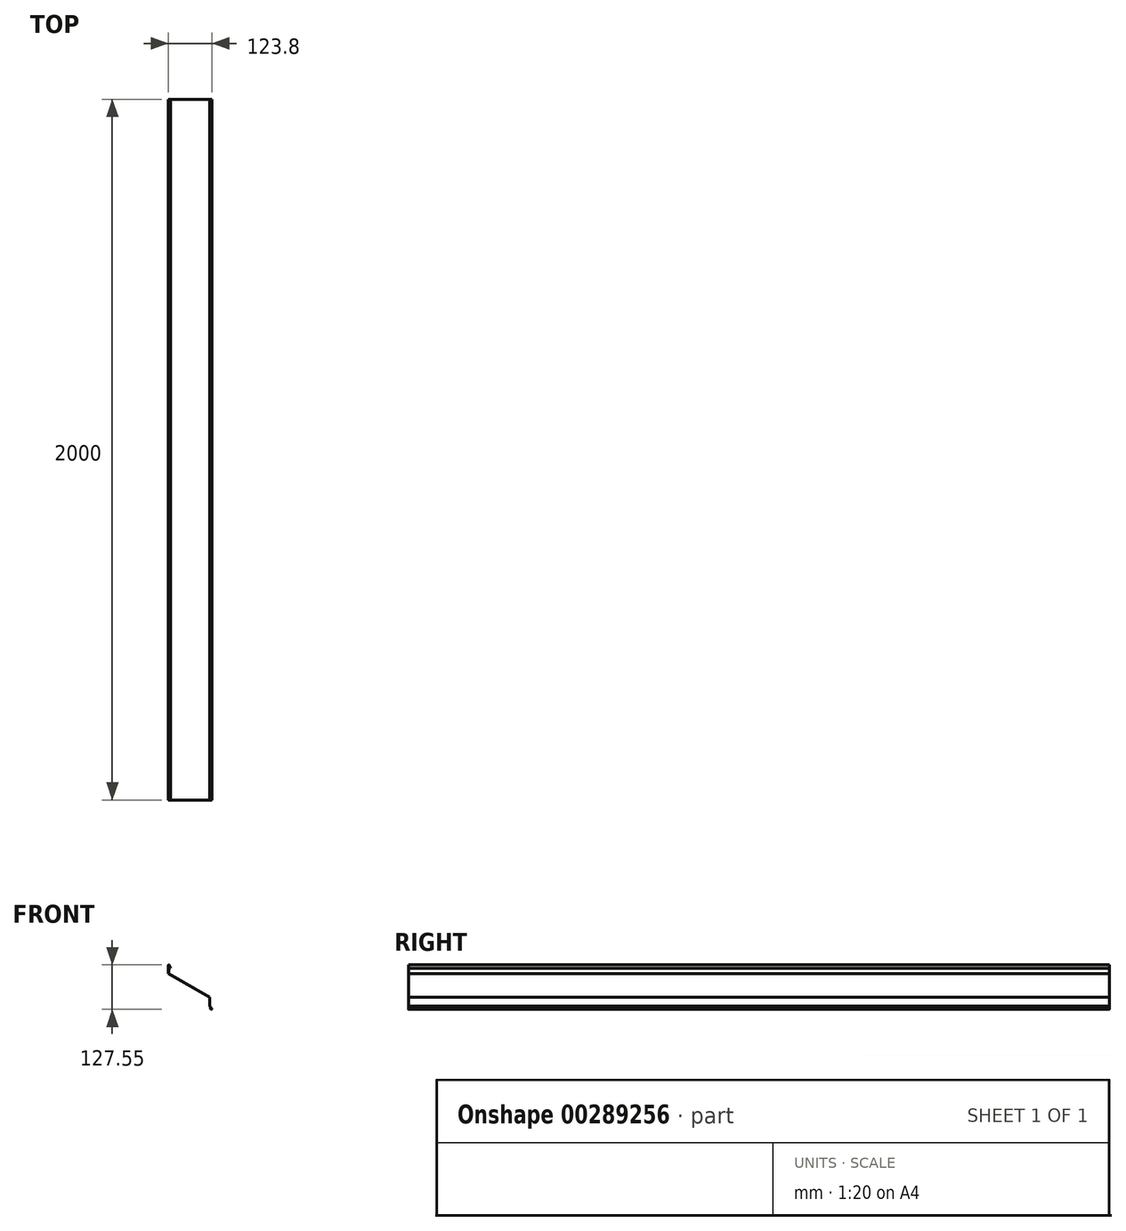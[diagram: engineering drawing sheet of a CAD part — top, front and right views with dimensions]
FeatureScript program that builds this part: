
annotation { "Feature Type Name" : "Feature", "Feature Type Description" : "" }
export const myFeature = defineFeature(function(context is Context, id is Id, definition is map)
    precondition{}
    {
        {
            var Q0;
            Q0=qCreatedBy(makeId("Front.planeOp"),FACE);
            var sketch = newSketch(context, id + "F0", { "sketchPlane" : qUnion([Q0])});
            skLineSegment(sketch, "E0", {"start": v(0, -1.3) * mm, "end": v(0, -25) * mm});
            skLineSegment(sketch, "E1", {"start": v(0, -25) * mm, "end": v(117, -92.55) * mm});
            skLineSegment(sketch, "E2", {"start": v(117, -92.55) * mm, "end": v(117, -117.55) * mm});
            skLineSegment(sketch, "E3", {"start": v(-1, -1.3) * mm, "end": v(-1, -25.58) * mm});
            skLineSegment(sketch, "E4", {"start": v(-1, -25.58) * mm, "end": v(116, -93.13) * mm});
            skLineSegment(sketch, "E5", {"start": v(116, -93.13) * mm, "end": v(116, -117.87) * mm});
            skLineSegment(sketch, "E6", {"start": v(117, -117.55) * mm, "end": v(122.57, -125.5) * mm});
            skLineSegment(sketch, "E7", {"start": v(121.75, -126.08) * mm, "end": v(116, -117.87) * mm});
            skArc(sketch, "E8", {"start": v(121.26, -126.42) * mm, "mid": v(121.68, -126.5) * mm, "end": v(121.75, -126.08) * mm});
            skArc(sketch, "E9", {"start": v(120.44, -127) * mm, "mid": v(122.25, -127.31) * mm, "end": v(122.57, -125.5) * mm});
            skLineSegment(sketch, "E10", {"start": v(121.35, -128.3) * mm, "end": v(116.6, -121.5) * mm});
            skLineSegment(sketch, "E11", {"start": v(116.6, -121.5) * mm, "end": v(117.42, -120.93) * mm});
            skLineSegment(sketch, "E12", {"start": v(117.42, -120.93) * mm, "end": v(121.26, -126.42) * mm});
            skPoint(sketch, "E13.start.orphan", {"position": v(125.11, -129.13) * mm});
            skArc(sketch, "E14", {"start": v(1.52, -0.85) * mm, "mid": v(0.07, -0.02) * mm, "end": v(-1, -1.3) * mm});
            skLineSegment(sketch, "E15", {"start": v(4.06, -10.65) * mm, "end": v(5, -10.3) * mm});
            skLineSegment(sketch, "E16", {"start": v(5, -10.3) * mm, "end": v(1.52, -0.85) * mm});
            skPoint(sketch, "E17.orphan", {"position": v(-1, -1.3) * mm});
            skArc(sketch, "E18", {"start": v(0.58, -1.2) * mm, "mid": v(0.25, -1) * mm, "end": v(0, -1.3) * mm});
            skLineSegment(sketch, "E19", {"start": v(4.06, -10.65) * mm, "end": v(0.58, -1.2) * mm});
            skSolve(sketch);
        }
        {
            var Q0;
            Q0 = qSketchRegion(id + "F0", true);
            extrude(context, id + "F1", {"entities" : qUnion([Q0]), "depth" : 2000 * mm});
        }
    });
